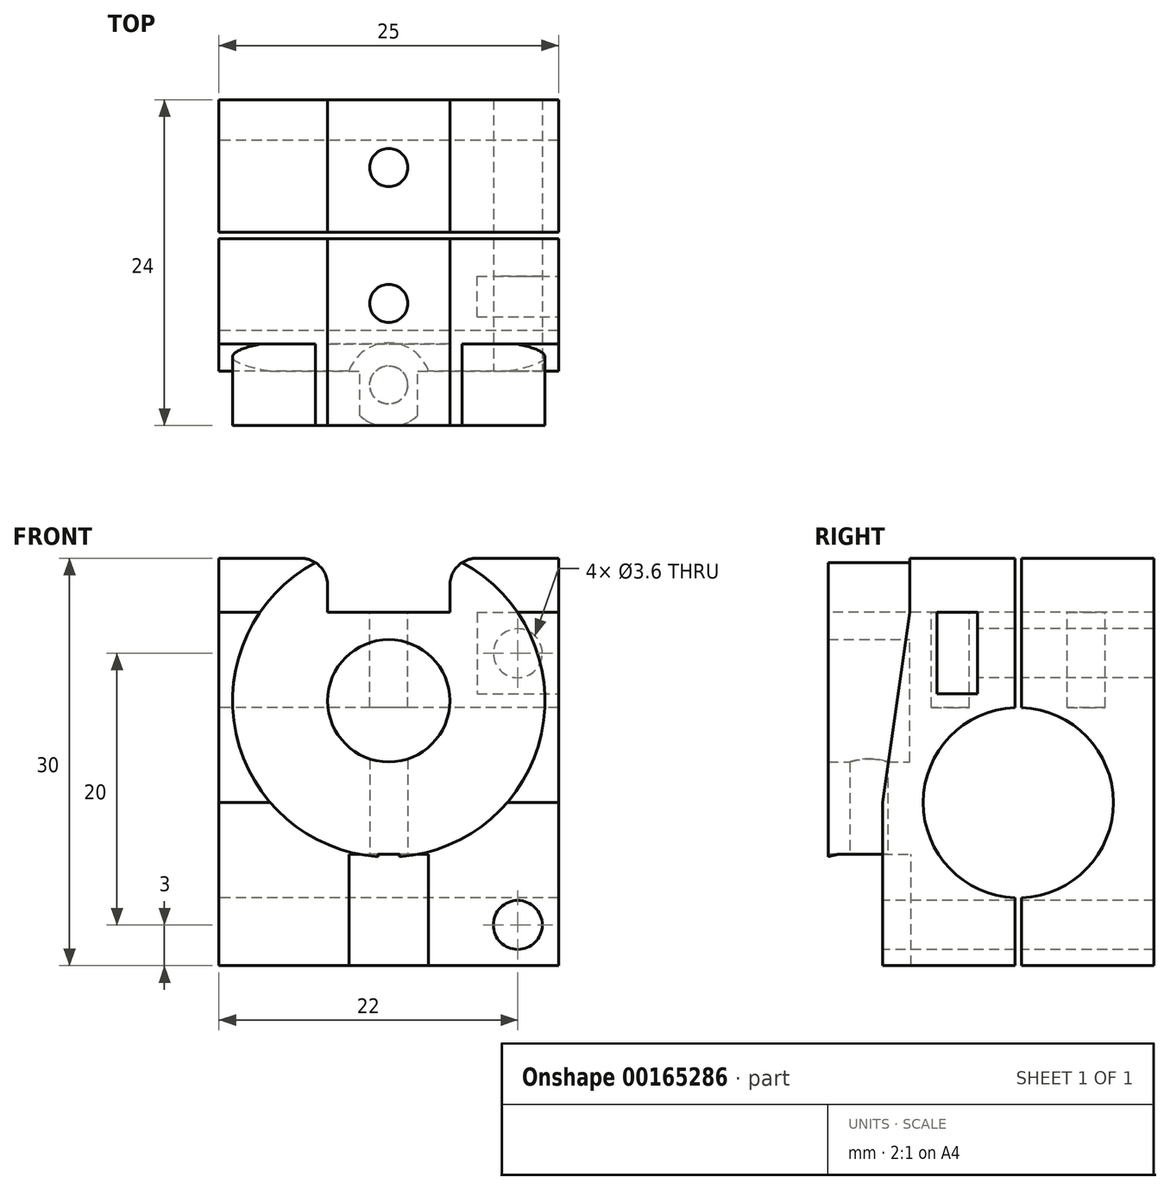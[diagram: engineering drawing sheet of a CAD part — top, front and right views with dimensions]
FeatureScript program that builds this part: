
annotation { "Feature Type Name" : "Feature", "Feature Type Description" : "" }
export const myFeature = defineFeature(function(context is Context, id is Id, definition is map)
    precondition{}
    {
        {
            var Q0;
            Q0=qCreatedBy(makeId("Right.planeOp"),FACE);
            var sketch = newSketch(context, id + "F0", { "sketchPlane" : qUnion([Q0])});
            skCircle(sketch, "E0", {"center": v(0, 0) * mm, "radius": 7 * mm});
            skLineSegment(sketch, "E1.bottom", {"start": v(-10, -12) * mm, "end": v(10, -12) * mm});
            skLineSegment(sketch, "E1.top", {"start": v(-8, 14) * mm, "end": v(10, 14) * mm});
            skLineSegment(sketch, "E1.left", {"start": v(-10, -12) * mm, "end": v(-10, 0) * mm});
            skLineSegment(sketch, "E1.right", {"start": v(10, -12) * mm, "end": v(10, 14) * mm});
            skLineSegment(sketch, "E2", {"start": v(-8, 14) * mm, "end": v(-10, 0) * mm});
            skSolve(sketch);
        }
        {
            var Q0;
            {var subQ2=sQuery(id+"F0.wireOp",EDGE,"E0");Q0=makeQuery(id+"F0.imprint","IMPRINT",FACE,{"disambiguationData":[TD([[makeQuery(id+"F0.imprint","IMPRINT",EDGE,{"derivedFrom":subQ2}),-1.0]])]});}
            extrude(context, id + "F1", {"entities" : qUnion([Q0]), "endBound" : BoundingType.SYMMETRIC, "depth" : 25 * mm});
        }
        {
            var Q0;
            Q0=makeQuery(id+"F1.opExtrude","SWEPT_FACE",FACE,{"disambiguationData":[OSD([sQuery(id+"F0.wireOp",EDGE,"E1.left")])]});
            cPlane(context, id + "F2", {"entities" : qUnion([Q0]), "cplaneType" : CPlaneType.OFFSET, "offset" : 1 * mm, "width" : 150 * mm, "height" : 150 * mm});
        }
        {
            var Q0;
            Q0=qCreatedBy(id+"F2.planeOp",FACE);
            var sketch = newSketch(context, id + "F3", { "sketchPlane" : qUnion([Q0])});
            skCircle(sketch, "E3", {"center": v(0, 7.5) * mm, "radius": 4.5 * mm});
            skCircle(sketch, "E4", {"center": v(0, 7.5) * mm, "radius": 11.5 * mm});
            skLineSegment(sketch, "E5", {"start": v(0, 7.5) * mm, "end": v(0, -4) * mm, "construction": true});
            skSolve(sketch);
        }
        {
            var Q0;
            Q0 = qSketchRegion(id + "F3", true);
            extrude(context, id + "F4", {"entities" : qUnion([Q0]), "operationType" : NewBodyOperationType.ADD, "endBound" : BoundingType.SYMMETRIC, "depth" : 6 * mm});
        }
        {
            var Q0;
            Q0=sQuery(id+"F3.wireOp",VERTEX,"E5.end");
            var Q1;
            Q1=sQuery(id+"F3.wireOp",EDGE,"E5");
            cPlane(context, id + "F5", {"entities" : qUnion([Q0, Q1]), "cplaneType" : CPlaneType.LINE_POINT, "offset" : 25 * mm, "width" : 150 * mm, "height" : 150 * mm});
        }
        {
            var Q0;
            Q0=qCreatedBy(id+"F5.planeOp",FACE);
            var sketch = newSketch(context, id + "F6", { "sketchPlane" : qUnion([Q0])});
            skPoint(sketch, "E6.0", {"position": v(0, 11) * mm});
            skCircle(sketch, "E7", {"center": v(0, 11) * mm, "radius": 1.4 * mm});
            skCircle(sketch, "E8", {"center": v(0, 11) * mm, "radius": 3.1 * mm});
            skSolve(sketch);
        }
        {
            var Q0;
            Q0=makeQuery(id+"F6.imprint","IMPRINT",FACE,{"disambiguationData":[TD([[makeQuery(id+"F6.imprint","IMPRINT",EDGE,{"derivedFrom":sQuery(id+"F6.wireOp",EDGE,"E7")}),1.0]])]});
            var Q1;
            Q1=makeQuery(id+"F4.opExtrude","SWEPT_FACE",FACE,{"disambiguationData":[OSD([sQuery(id+"F3.wireOp",EDGE,"E3")])]});
            extrude(context, id + "F7", {"entities" : qUnion([Q0]), "operationType" : NewBodyOperationType.REMOVE, "endBound" : BoundingType.UP_TO_SURFACE, "oppositeDirection" : true, "endBoundEntityFace" : qUnion([Q1]), "depth" : 25 * mm});
        }
        {
            var Q0;
            Q0=makeQuery(id+"F6.imprint","IMPRINT",FACE,{"disambiguationData":[TD([[makeQuery(id+"F6.imprint","IMPRINT",EDGE,{"derivedFrom":sQuery(id+"F6.wireOp",EDGE,"E7")}),-1.0]])]});
            var Q1;
            Q1=makeQuery(id+"F6.imprint","IMPRINT",FACE,{"disambiguationData":[TD([[makeQuery(id+"F6.imprint","IMPRINT",EDGE,{"derivedFrom":sQuery(id+"F6.wireOp",EDGE,"E7")}),1.0]])]});
            extrude(context, id + "F8", {"entities" : qUnion([Q0, Q1]), "operationType" : NewBodyOperationType.REMOVE, "endBound" : BoundingType.THROUGH_ALL, "depth" : 25 * mm, "hasSecondDirection" : true, "secondDirectionOppositeDirection" : true, "secondDirectionDepth" : 0.2 * mm});
        }
        {
            var Q0;
            Q0=sQuery(id+"F3.wireOp",VERTEX,"E5.start");
            var Q1;
            Q1=qCreatedBy(makeId("Top.planeOp"),FACE);
            cPlane(context, id + "F9", {"entities" : qUnion([Q0, Q1]), "cplaneType" : CPlaneType.PLANE_POINT, "offset" : 25 * mm, "width" : 150 * mm, "height" : 150 * mm});
        }
        {
            var Q0;
            Q0=qCreatedBy(id+"F9.planeOp",FACE);
            var sketch = newSketch(context, id + "F10", { "sketchPlane" : qUnion([Q0])});
            skLineSegment(sketch, "E9", {"start": v(0, -22.3) * mm, "end": v(0, -85.85) * mm, "construction": true});
            skSolve(sketch);
        }
        {
            var Q0;
            Q0=makeQuery(id+"F3.imprint","IMPRINT",FACE,{"disambiguationData":[TD([[makeQuery(id+"F3.imprint","IMPRINT",EDGE,{"derivedFrom":sQuery(id+"F3.wireOp",EDGE,"E3")}),1.0]])]});
            var Q1;
            Q1=sQuery(id+"F3.wireOp",EDGE,"E3");
            extrude(context, id + "F11", {"entities" : qUnion([Q0]), "operationType" : NewBodyOperationType.REMOVE, "surfaceEntities" : qUnion([Q1]), "endBound" : BoundingType.SYMMETRIC, "oppositeDirection" : true, "depth" : 6 * mm});
        }
        {
            var Q0;
            Q0=makeQuery(id+"F1.opExtrude","SWEPT_FACE",FACE,{"disambiguationData":[OSD([sQuery(id+"F0.wireOp",EDGE,"E1.top")])]});
            var sketch = newSketch(context, id + "F12", { "sketchPlane" : qUnion([Q0])});
            skLineSegment(sketch, "E10.bottom", {"start": v(-12.5, 10) * mm, "end": v(-4.5, 10) * mm});
            skLineSegment(sketch, "E10.top", {"start": v(-12.5, -8) * mm, "end": v(-4.5, -8) * mm});
            skLineSegment(sketch, "E10.left", {"start": v(-12.5, 10) * mm, "end": v(-12.5, -8) * mm});
            skLineSegment(sketch, "E10.right", {"start": v(-4.5, 10) * mm, "end": v(-4.5, -8) * mm});
            skLineSegment(sketch, "E11.bottom", {"start": v(12.5, 10) * mm, "end": v(4.5, 10) * mm});
            skLineSegment(sketch, "E11.top", {"start": v(12.5, -8) * mm, "end": v(4.5, -8) * mm});
            skLineSegment(sketch, "E11.left", {"start": v(12.5, 10) * mm, "end": v(12.5, -8) * mm});
            skLineSegment(sketch, "E11.right", {"start": v(4.5, 10) * mm, "end": v(4.5, -8) * mm});
            skSolve(sketch);
        }
        {
            var Q0;
            Q0 = qSketchRegion(id + "F12", true);
            extrude(context, id + "F13", {"entities" : qUnion([Q0]), "operationType" : NewBodyOperationType.ADD, "depth" : 4 * mm});
        }
        {
            var Q0;
            Q0=makeQuery(id+"F13.opExtrude","CAP_EDGE",EDGE,{"disambiguationData":[OSD([sQuery(id+"F12.wireOp",EDGE,"E10.right")])],"isStart":false});
            var Q1;
            Q1=makeQuery(id+"F13.opExtrude","CAP_EDGE",EDGE,{"disambiguationData":[OSD([sQuery(id+"F12.wireOp",EDGE,"E11.right")])],"isStart":false});
            fillet(context, id + "F14", {"entities" : qUnion([Q0, Q1]), "radius" : 2 * mm, "tangentPropagation" : true, "allowEdgeOverflow" : false});
        }
        {
            var Q0;
            Q0=makeQuery(id+"F4.opExtrude","CAP_FACE",FACE,{"disambiguationData":[OSD([sQuery(id+"F3.wireOp",EDGE,"E3"),sQuery(id+"F3.wireOp",EDGE,"E4")])],"isStart":true});
            extrude(context, id + "F15", {"entities" : qUnion([Q0]), "operationType" : NewBodyOperationType.REMOVE, "endBound" : BoundingType.THROUGH_ALL, "oppositeDirection" : true, "depth" : 25 * mm});
        }
        {
            var Q0;
            {var subQ0=sQuery(id+"F0.wireOp",EDGE,"E1.top");Q0=makeQuery(id+"F15.boolean.opBoolean","MERGE",FACE,{"derivedFrom":[makeQuery(id+"F1.opExtrude","SWEPT_FACE",FACE,{"disambiguationData":[OSD([subQ0])]}),makeQuery(id+"F15.opExtrude","SWEPT_FACE",FACE,{"disambiguationData":[OSD([subQ0,sQuery(id+"F0.wireOp",EDGE,"E2")])]})]});}
            var sketch = newSketch(context, id + "F16", { "sketchPlane" : qUnion([Q0])});
            skLineSegment(sketch, "E12", {"start": v(15.75, 0) * mm, "end": v(-19.54, 0) * mm, "construction": true});
            skCircle(sketch, "E13", {"center": v(0, 5) * mm, "radius": 1.4 * mm});
            skCircle(sketch, "E14.MirrorC", {"center": v(0, -5) * mm, "radius": 1.4 * mm});
            skSolve(sketch);
        }
        {
            var Q0;
            Q0 = qSketchRegion(id + "F16", true);
            extrude(context, id + "F17", {"entities" : qUnion([Q0]), "operationType" : NewBodyOperationType.REMOVE, "oppositeDirection" : true, "depth" : 7 * mm});
        }
        {
            var Q0;
            Q0=makeQuery(id+"F13.boolean.opBoolean","MERGE",FACE,{"derivedFrom":[makeQuery(id+"F1.opExtrude","CAP_FACE",FACE,{"disambiguationData":[OSD([sQuery(id+"F0.wireOp",EDGE,"E0"),sQuery(id+"F0.wireOp",EDGE,"E1.bottom"),sQuery(id+"F0.wireOp",EDGE,"E1.top"),sQuery(id+"F0.wireOp",EDGE,"E1.left"),sQuery(id+"F0.wireOp",EDGE,"E1.right"),sQuery(id+"F0.wireOp",EDGE,"E2")])],"isStart":false}),makeQuery(id+"F13.opExtrude","SWEPT_FACE",FACE,{"disambiguationData":[OSD([sQuery(id+"F12.wireOp",EDGE,"E11.left")])]})]});
            var sketch = newSketch(context, id + "F18", { "sketchPlane" : qUnion([Q0])});
            skLineSegment(sketch, "E15", {"start": v(0, -3.32) * mm, "end": v(0, 43.87) * mm, "construction": true});
            skLineSegment(sketch, "E16.bottom", {"start": v(-6, 14) * mm, "end": v(-3, 14) * mm});
            skLineSegment(sketch, "E16.top", {"start": v(-6, 8) * mm, "end": v(-3, 8) * mm});
            skLineSegment(sketch, "E16.left", {"start": v(-6, 14) * mm, "end": v(-6, 8) * mm});
            skLineSegment(sketch, "E16.right", {"start": v(-3, 14) * mm, "end": v(-3, 8) * mm});
            skSolve(sketch);
        }
        {
            var Q0;
            Q0=makeQuery(id+"F18.imprint","IMPRINT",FACE,{"disambiguationData":[TD([[makeQuery(id+"F18.imprint","IMPRINT",EDGE,{"derivedFrom":sQuery(id+"F18.wireOp",EDGE,"E16.bottom")}),-1.0]])]});
            extrude(context, id + "F19", {"entities" : qUnion([Q0]), "operationType" : NewBodyOperationType.REMOVE, "oppositeDirection" : true, "depth" : 6 * mm});
        }
        {
            var Q0;
            Q0=makeQuery(id+"F19.boolean.opBoolean","COPY",FACE,{"derivedFrom":makeQuery(id+"F19.opExtrude","SWEPT_FACE",FACE,{"disambiguationData":[OSD([sQuery(id+"F18.wireOp",EDGE,"E16.right")])]})});
            var sketch = newSketch(context, id + "F20", { "sketchPlane" : qUnion([Q0])});
            skLineSegment(sketch, "E17", {"start": v(12.5, 14) * mm, "end": v(6.5, 8) * mm, "construction": true});
            skCircle(sketch, "E18", {"center": v(9.5, 11) * mm, "radius": 1.8 * mm});
            skSolve(sketch);
        }
        {
            var Q0;
            Q0=makeQuery(id+"F20.imprint","IMPRINT",FACE,{"disambiguationData":[TD([[makeQuery(id+"F20.imprint","IMPRINT",EDGE,{"derivedFrom":sQuery(id+"F20.wireOp",EDGE,"E18")}),1.0]])]});
            extrude(context, id + "F21", {"entities" : qUnion([Q0]), "operationType" : NewBodyOperationType.REMOVE, "endBound" : BoundingType.THROUGH_ALL, "oppositeDirection" : true, "depth" : 25 * mm});
        }
        {
            var Q0;
            {var subQ1=sQuery(id+"F0.wireOp",EDGE,"E2");var subQ2=sQuery(id+"F0.wireOp",EDGE,"E1.bottom");var subQ3=sQuery(id+"F0.wireOp",EDGE,"E1.left");Q0=makeQuery(id+"F8.boolean.opBoolean","SPLIT",FACE,{"disambiguationData":[TD([makeQuery(id+"F1.opExtrude","CAP_FACE",FACE,{"disambiguationData":[OSD([sQuery(id+"F0.wireOp",EDGE,"E0"),subQ2,sQuery(id+"F0.wireOp",EDGE,"E1.top"),subQ3,sQuery(id+"F0.wireOp",EDGE,"E1.right"),subQ1])],"isStart":false})])],"derivedFrom":makeQuery(id+"F1.opExtrude","SWEPT_FACE",FACE,{"disambiguationData":[OSD([subQ3])]})});}
            var sketch = newSketch(context, id + "F22", { "sketchPlane" : qUnion([Q0])});
            skCircle(sketch, "E19", {"center": v(9.5, -9) * mm, "radius": 1.8 * mm});
            skSolve(sketch);
        }
        {
            var Q0;
            Q0=makeQuery(id+"F22.imprint","IMPRINT",FACE,{"disambiguationData":[TD([[makeQuery(id+"F22.imprint","IMPRINT",EDGE,{"derivedFrom":sQuery(id+"F22.wireOp",EDGE,"E19")}),1.0]])]});
            extrude(context, id + "F23", {"entities" : qUnion([Q0]), "operationType" : NewBodyOperationType.REMOVE, "endBound" : BoundingType.THROUGH_ALL, "oppositeDirection" : true, "depth" : 25 * mm});
        }
        {
            var Q0;
            Q0=makeQuery(id+"F13.boolean.opBoolean","MERGE",FACE,{"derivedFrom":[makeQuery(id+"F1.opExtrude","CAP_FACE",FACE,{"disambiguationData":[OSD([sQuery(id+"F0.wireOp",EDGE,"E0"),sQuery(id+"F0.wireOp",EDGE,"E1.bottom"),sQuery(id+"F0.wireOp",EDGE,"E1.top"),sQuery(id+"F0.wireOp",EDGE,"E1.left"),sQuery(id+"F0.wireOp",EDGE,"E1.right"),sQuery(id+"F0.wireOp",EDGE,"E2")])],"isStart":false}),makeQuery(id+"F13.opExtrude","SWEPT_FACE",FACE,{"disambiguationData":[OSD([sQuery(id+"F12.wireOp",EDGE,"E11.left")])]})]});
            var sketch = newSketch(context, id + "F24", { "sketchPlane" : qUnion([Q0])});
            skLineSegment(sketch, "E20", {"start": v(0, -16) * mm, "end": v(0, 26.67) * mm, "construction": true});
            skLineSegment(sketch, "E21.bottom", {"start": v(-0.25, 19.14) * mm, "end": v(0.25, 19.14) * mm});
            skLineSegment(sketch, "E21.top", {"start": v(-0.25, -13.94) * mm, "end": v(0.25, -13.94) * mm});
            skLineSegment(sketch, "E21.left", {"start": v(-0.25, 19.14) * mm, "end": v(-0.25, -13.94) * mm});
            skLineSegment(sketch, "E21.right", {"start": v(0.25, 19.14) * mm, "end": v(0.25, -13.94) * mm});
            skSolve(sketch);
        }
        {
            var Q0;
            Q0 = qSketchRegion(id + "F24", true);
            extrude(context, id + "F25", {"entities" : qUnion([Q0]), "operationType" : NewBodyOperationType.REMOVE, "endBound" : BoundingType.THROUGH_ALL, "oppositeDirection" : true, "depth" : 25 * mm});
        }
    });
